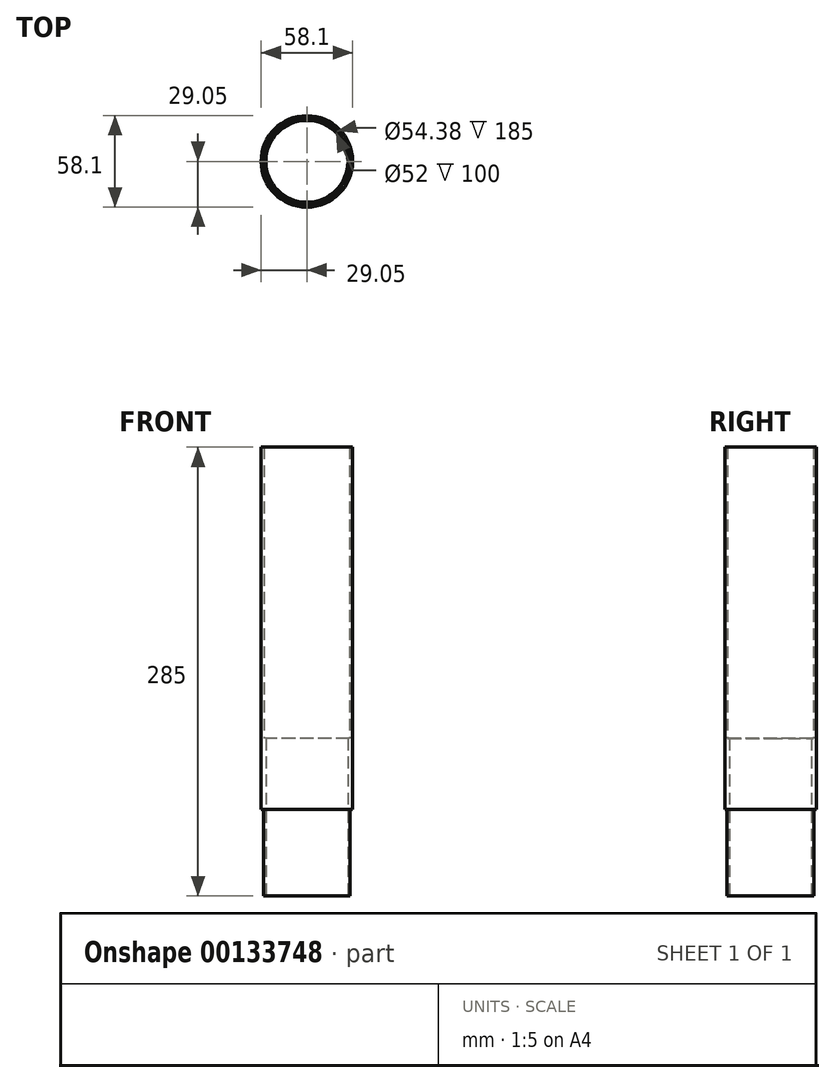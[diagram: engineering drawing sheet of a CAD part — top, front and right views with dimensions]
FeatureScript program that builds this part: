
annotation { "Feature Type Name" : "Feature", "Feature Type Description" : "" }
export const myFeature = defineFeature(function(context is Context, id is Id, definition is map)
    precondition{}
    {
        {
            var Q0;
            Q0=qCreatedBy(makeId("Top.planeOp"),FACE);
            var sketch = newSketch(context, id + "F0", { "sketchPlane" : qUnion([Q0])});
            skCircle(sketch, "E0", {"center": v(0, 0) * mm, "radius": 27.2 * mm});
            skCircle(sketch, "E1", {"center": v(0, 0) * mm, "radius": 29.05 * mm});
            skSolve(sketch);
        }
        {
            var Q0;
            Q0 = qSketchRegion(id + "F0", true);
            extrude(context, id + "F1", {"entities" : qUnion([Q0]), "depth" : 230 * mm});
        }
        {
            var Q0;
            Q0=qCreatedBy(makeId("Front.planeOp"),FACE);
            var sketch = newSketch(context, id + "F2", { "sketchPlane" : qUnion([Q0])});
            skLineSegment(sketch, "E2.bottom", {"start": v(-2.5, 165) * mm, "end": v(2.5, 165) * mm});
            skLineSegment(sketch, "E2.top", {"start": v(-2.5, 65) * mm, "end": v(2.5, 65) * mm});
            skLineSegment(sketch, "E2.left", {"start": v(-2.5, 165) * mm, "end": v(-2.5, 65) * mm});
            skLineSegment(sketch, "E2.right", {"start": v(2.5, 165) * mm, "end": v(2.5, 65) * mm});
            skPoint(sketch, "E3", {"position": v(0, 65) * mm});
            skPoint(sketch, "E4", {"position": v(-2.5, 115) * mm});
            skSolve(sketch);
        }
        {
            var Q0;
            Q0=qCreatedBy(makeId("Top.planeOp"),FACE);
            var sketch = newSketch(context, id + "F3", { "sketchPlane" : qUnion([Q0])});
            skCircle(sketch, "E5", {"center": v(0, 0) * mm, "radius": 27.5 * mm});
            skCircle(sketch, "E6", {"center": v(0, 0) * mm, "radius": 26 * mm});
            skSolve(sketch);
        }
        {
            var Q0;
            Q0 = qSketchRegion(id + "F3", true);
            extrude(context, id + "F4", {"entities" : qUnion([Q0]), "operationType" : NewBodyOperationType.ADD, "depth" : 45 * mm, "hasSecondDirection" : true, "secondDirectionOppositeDirection" : true, "secondDirectionDepth" : 55 * mm});
        }
    });
